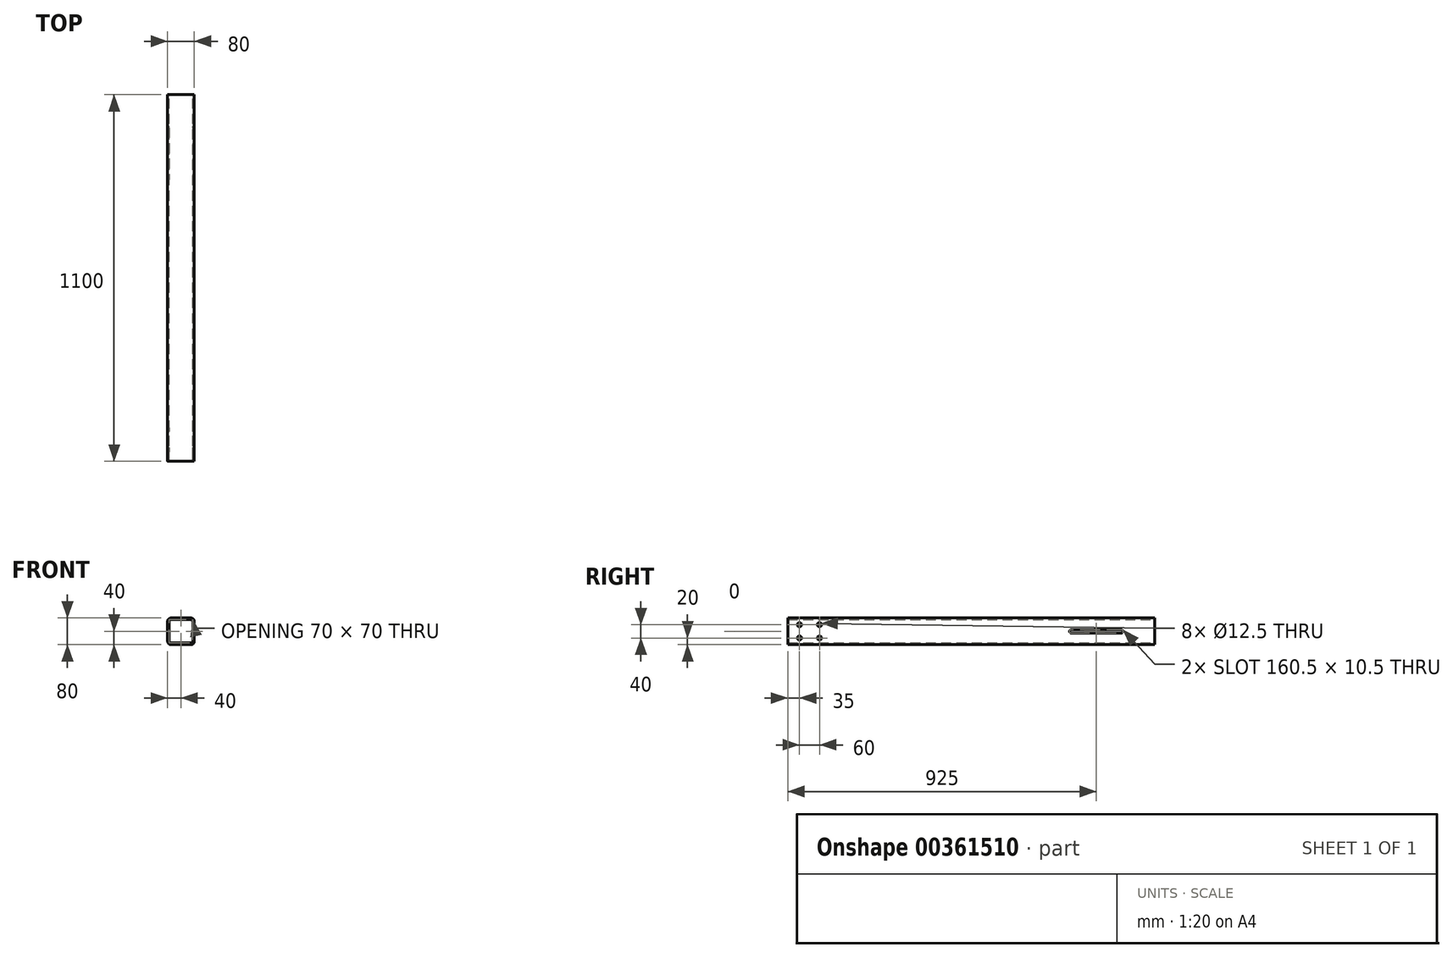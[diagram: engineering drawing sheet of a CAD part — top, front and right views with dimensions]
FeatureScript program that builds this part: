
annotation { "Feature Type Name" : "Feature", "Feature Type Description" : "" }
export const myFeature = defineFeature(function(context is Context, id is Id, definition is map)
    precondition{}
    {
        {
            var Q0;
            Q0=qCreatedBy(makeId("Front.planeOp"),FACE);
            var sketch = newSketch(context, id + "F0", { "sketchPlane" : qUnion([Q0])});
            skLineSegment(sketch, "E0.bottom", {"start": v(30, 40) * mm, "end": v(-30, 40) * mm});
            skLineSegment(sketch, "E0.top", {"start": v(30, -40) * mm, "end": v(-30, -40) * mm});
            skLineSegment(sketch, "E0.left", {"start": v(40, 30) * mm, "end": v(40, -30) * mm});
            skLineSegment(sketch, "E0.right", {"start": v(-40, 30) * mm, "end": v(-40, -30) * mm});
            skPoint(sketch, "E0.middle", {"position": v(0, 0) * mm});
            skPoint(sketch, "E1.visualSharp", {"position": v(-40, 40) * mm});
            skArc(sketch, "E1.filletArc", {"start": v(-30, 40) * mm, "mid": v(-37.07, 37.07) * mm, "end": v(-40, 30) * mm});
            skPoint(sketch, "E2.visualSharp", {"position": v(40, 40) * mm});
            skArc(sketch, "E2.filletArc", {"start": v(40, 30) * mm, "mid": v(37.07, 37.07) * mm, "end": v(30, 40) * mm});
            skPoint(sketch, "E3.visualSharp", {"position": v(40, -40) * mm});
            skArc(sketch, "E3.filletArc", {"start": v(30, -40) * mm, "mid": v(37.07, -37.07) * mm, "end": v(40, -30) * mm});
            skPoint(sketch, "E4.visualSharp", {"position": v(-40, -40) * mm});
            skArc(sketch, "E4.filletArc", {"start": v(-40, -30) * mm, "mid": v(-37.07, -37.07) * mm, "end": v(-30, -40) * mm});
            skArc(sketch, "E5.0", {"start": v(35, 30) * mm, "mid": v(33.54, 33.54) * mm, "end": v(30, 35) * mm});
            skLineSegment(sketch, "E5.1", {"start": v(35, 30) * mm, "end": v(35, -30) * mm});
            skLineSegment(sketch, "E5.2", {"start": v(30, 35) * mm, "end": v(-30, 35) * mm});
            skArc(sketch, "E5.3", {"start": v(30, -35) * mm, "mid": v(33.54, -33.54) * mm, "end": v(35, -30) * mm});
            skArc(sketch, "E5.4", {"start": v(-30, 35) * mm, "mid": v(-33.54, 33.54) * mm, "end": v(-35, 30) * mm});
            skLineSegment(sketch, "E5.5", {"start": v(-35, 30) * mm, "end": v(-35, -30) * mm});
            skArc(sketch, "E5.6", {"start": v(-35, -30) * mm, "mid": v(-33.54, -33.54) * mm, "end": v(-30, -35) * mm});
            skLineSegment(sketch, "E5.7", {"start": v(30, -35) * mm, "end": v(-30, -35) * mm});
            skSolve(sketch);
        }
        {
            var Q0;
            Q0 = qSketchRegion(id + "F0", true);
            extrude(context, id + "F1", {"entities" : qUnion([Q0]), "endBound" : BoundingType.SYMMETRIC, "depth" : 1100 * mm});
        }
        {
            var Q0;
            Q0=makeQuery(id+"F1.opExtrude","SWEPT_FACE",FACE,{"disambiguationData":[OSD([sQuery(id+"F0.wireOp",EDGE,"E0.left")])]});
            var sketch = newSketch(context, id + "F2", { "sketchPlane" : qUnion([Q0])});
            skLineSegment(sketch, "E6", {"start": v(-550, 0) * mm, "end": v(-485, 0) * mm, "construction": true});
            skLineSegment(sketch, "E7.bottom", {"start": v(-515, 20) * mm, "end": v(-455, 20) * mm, "construction": true});
            skLineSegment(sketch, "E7.top", {"start": v(-515, -20) * mm, "end": v(-455, -20) * mm, "construction": true});
            skLineSegment(sketch, "E7.left", {"start": v(-515, 20) * mm, "end": v(-515, -20) * mm, "construction": true});
            skLineSegment(sketch, "E7.right", {"start": v(-455, 20) * mm, "end": v(-455, -20) * mm, "construction": true});
            skPoint(sketch, "E7.middle", {"position": v(-485, 0) * mm});
            skCircle(sketch, "E8", {"center": v(-515, 20) * mm, "radius": 6.25 * mm});
            skCircle(sketch, "E9", {"center": v(-515, -20) * mm, "radius": 6.25 * mm});
            skCircle(sketch, "E10", {"center": v(-455, 20) * mm, "radius": 6.25 * mm});
            skCircle(sketch, "E11", {"center": v(-455, -20) * mm, "radius": 6.25 * mm});
            skSolve(sketch);
        }
        {
            var Q0;
            Q0 = qSketchRegion(id + "F2", true);
            extrude(context, id + "F3", {"entities" : qUnion([Q0]), "operationType" : NewBodyOperationType.REMOVE, "endBound" : BoundingType.THROUGH_ALL, "oppositeDirection" : true, "depth" : 25 * mm});
        }
        {
            var Q0;
            Q0=makeQuery(id+"F1.opExtrude","SWEPT_FACE",FACE,{"disambiguationData":[OSD([sQuery(id+"F0.wireOp",EDGE,"E0.left")])]});
            var sketch = newSketch(context, id + "F4", { "sketchPlane" : qUnion([Q0])});
            skLineSegment(sketch, "E12", {"start": v(550, 0) * mm, "end": v(375, 0) * mm, "construction": true});
            skPoint(sketch, "E12.endSnap0", {"position": v(550, 0) * mm});
            skLineSegment(sketch, "E13.bottom", {"start": v(450, 5.25) * mm, "end": v(300, 5.25) * mm});
            skLineSegment(sketch, "E13.top", {"start": v(450, -5.25) * mm, "end": v(300, -5.25) * mm});
            skLineSegment(sketch, "E13.left", {"start": v(450, 5.25) * mm, "end": v(450, -5.25) * mm, "construction": true});
            skLineSegment(sketch, "E13.right", {"start": v(300, 5.25) * mm, "end": v(300, -5.25) * mm, "construction": true});
            skPoint(sketch, "E13.middle", {"position": v(375, 0) * mm});
            skArc(sketch, "E14", {"start": v(300, 5.25) * mm, "mid": v(294.75, 0) * mm, "end": v(300, -5.25) * mm});
            skArc(sketch, "E15", {"start": v(450, -5.25) * mm, "mid": v(455.25, 0) * mm, "end": v(450, 5.25) * mm});
            skSolve(sketch);
        }
        {
            var Q0;
            Q0 = qSketchRegion(id + "F4", true);
            extrude(context, id + "F5", {"entities" : qUnion([Q0]), "operationType" : NewBodyOperationType.REMOVE, "endBound" : BoundingType.THROUGH_ALL, "oppositeDirection" : true, "depth" : 25 * mm});
        }
    });
